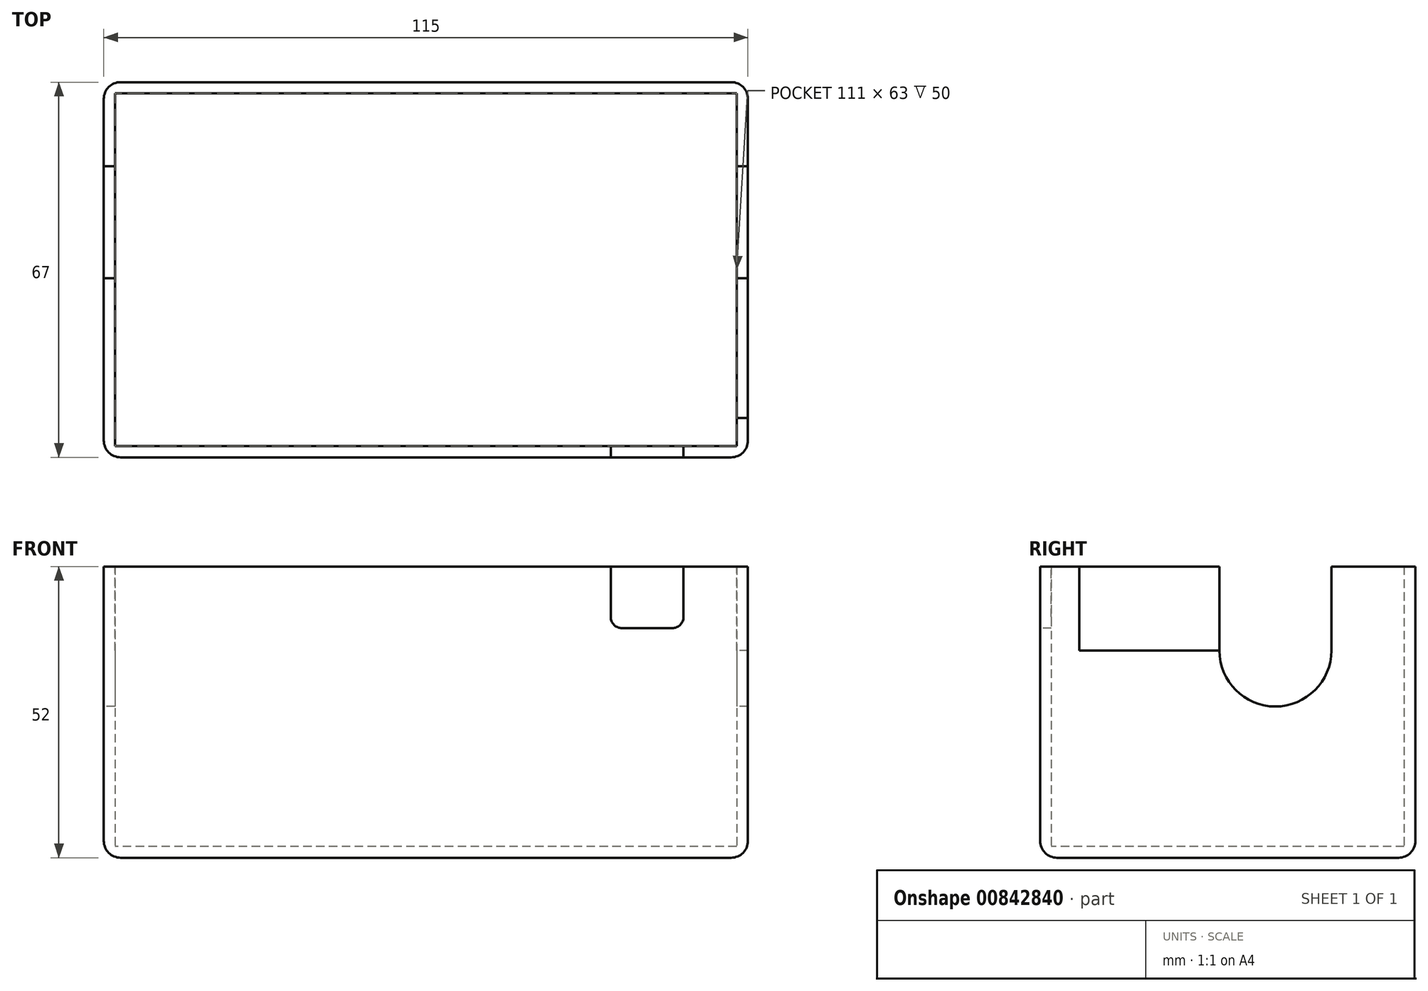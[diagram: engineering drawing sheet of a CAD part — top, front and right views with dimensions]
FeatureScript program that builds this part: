
annotation { "Feature Type Name" : "Feature", "Feature Type Description" : "" }
export const myFeature = defineFeature(function(context is Context, id is Id, definition is map)
    precondition{}
    {
        {
            var Q0;
            Q0=qCreatedBy(makeId("Top.planeOp"),FACE);
            var sketch = newSketch(context, id + "F0", { "sketchPlane" : qUnion([Q0])});
            skLineSegment(sketch, "E0.bottom", {"start": v(57.5, 33.5) * mm, "end": v(-57.5, 33.5) * mm});
            skLineSegment(sketch, "E0.top", {"start": v(57.5, -33.5) * mm, "end": v(-57.5, -33.5) * mm});
            skLineSegment(sketch, "E0.left", {"start": v(57.5, 33.5) * mm, "end": v(57.5, -33.5) * mm});
            skLineSegment(sketch, "E0.right", {"start": v(-57.5, 33.5) * mm, "end": v(-57.5, -33.5) * mm});
            skPoint(sketch, "E0.middle", {"position": v(0, 0) * mm});
            skSolve(sketch);
        }
        {
            var Q0;
            Q0=makeQuery(id+"F0.imprint","IMPRINT",FACE,{"disambiguationData":[TD([[makeQuery(id+"F0.imprint","IMPRINT",EDGE,{"derivedFrom":sQuery(id+"F0.wireOp",EDGE,"E0.bottom")}),1.0]])]});
            extrude(context, id + "F1", {"entities" : qUnion([Q0]), "depth" : 52 * mm, "offsetDistance" : 25 * mm});
        }
        {
            var Q0;
            Q0=makeQuery(id+"F1.opExtrude","CAP_FACE",FACE,{"disambiguationData":[OSD([sQuery(id+"F0.wireOp",EDGE,"E0.bottom"),sQuery(id+"F0.wireOp",EDGE,"E0.top"),sQuery(id+"F0.wireOp",EDGE,"E0.left"),sQuery(id+"F0.wireOp",EDGE,"E0.right")])],"isStart":false});
            shell(context, id + "F2", {"entities" : qUnion([Q0]), "thickness" : 2 * mm});
        }
        {
            var Q0;
            Q0=makeQuery(id+"F1.opExtrude","SWEPT_EDGE",EDGE,{"disambiguationData":[OSD([sQuery(id+"F0.wireOp",EDGE,"E0.bottom"),sQuery(id+"F0.wireOp",EDGE,"E0.left")])]});
            var Q1;
            Q1=makeQuery(id+"F1.opExtrude","SWEPT_EDGE",EDGE,{"disambiguationData":[OSD([sQuery(id+"F0.wireOp",EDGE,"E0.top"),sQuery(id+"F0.wireOp",EDGE,"E0.left")])]});
            var Q2;
            Q2=makeQuery(id+"F1.opExtrude","SWEPT_EDGE",EDGE,{"disambiguationData":[OSD([sQuery(id+"F0.wireOp",EDGE,"E0.top"),sQuery(id+"F0.wireOp",EDGE,"E0.right")])]});
            var Q3;
            Q3=makeQuery(id+"F1.opExtrude","SWEPT_EDGE",EDGE,{"disambiguationData":[OSD([sQuery(id+"F0.wireOp",EDGE,"E0.bottom"),sQuery(id+"F0.wireOp",EDGE,"E0.right")])]});
            var Q4;
            Q4=makeQuery(id+"F1.opExtrude","CAP_EDGE",EDGE,{"disambiguationData":[OSD([sQuery(id+"F0.wireOp",EDGE,"E0.right")])],"isStart":true});
            var Q5;
            Q5=makeQuery(id+"F1.opExtrude","CAP_EDGE",EDGE,{"disambiguationData":[OSD([sQuery(id+"F0.wireOp",EDGE,"E0.top")])],"isStart":true});
            var Q6;
            Q6=makeQuery(id+"F1.opExtrude","CAP_EDGE",EDGE,{"disambiguationData":[OSD([sQuery(id+"F0.wireOp",EDGE,"E0.bottom")])],"isStart":true});
            var Q7;
            Q7=makeQuery(id+"F1.opExtrude","CAP_EDGE",EDGE,{"disambiguationData":[OSD([sQuery(id+"F0.wireOp",EDGE,"E0.left")])],"isStart":true});
            fillet(context, id + "F3", {"entities" : qUnion([Q0, Q1, Q2, Q3, Q4, Q5, Q6, Q7]), "radius" : 3 * mm, "tangentPropagation" : true, "allowEdgeOverflow" : false});
        }
        {
            var Q0;
            Q0=makeQuery(id+"F1.opExtrude","SWEPT_FACE",FACE,{"disambiguationData":[OSD([sQuery(id+"F0.wireOp",EDGE,"E0.right")])]});
            var sketch = newSketch(context, id + "F4", { "sketchPlane" : qUnion([Q0])});
            skLineSegment(sketch, "E1", {"start": v(-33.5, 52) * mm, "end": v(-8.5, 52) * mm});
            skLineSegment(sketch, "E2", {"start": v(-8.5, 52) * mm, "end": v(-8.5, 37) * mm});
            skArc(sketch, "E3", {"start": v(-18.5, 37) * mm, "mid": v(-8.5, 27) * mm, "end": v(1.5, 37) * mm});
            skLineSegment(sketch, "E4", {"start": v(-18.5, 52) * mm, "end": v(-18.5, 37) * mm});
            skLineSegment(sketch, "E5", {"start": v(1.5, 52) * mm, "end": v(1.5, 37) * mm});
            skSolve(sketch);
        }
        {
            var Q0;
            Q0=makeQuery(id+"F4.imprint","IMPRINT",FACE,{"disambiguationData":[TD([[makeQuery(id+"F4.imprint","IMPRINT",EDGE,{"derivedFrom":sQuery(id+"F4.wireOp",EDGE,"E3")}),1.0]])]});
            var Q1;
            Q1=makeQuery(id+"F1.opExtrude","SWEPT_FACE",FACE,{"disambiguationData":[OSD([sQuery(id+"F0.wireOp",EDGE,"E0.left")])]});
            extrude(context, id + "F5", {"entities" : qUnion([Q0]), "operationType" : NewBodyOperationType.REMOVE, "endBound" : BoundingType.UP_TO_SURFACE, "oppositeDirection" : true, "depth" : 25 * mm, "endBoundEntityFace" : qUnion([Q1]), "offsetDistance" : 25 * mm});
        }
        {
            var Q0;
            Q0=makeQuery(id+"F1.opExtrude","SWEPT_FACE",FACE,{"disambiguationData":[OSD([sQuery(id+"F0.wireOp",EDGE,"E0.left")])]});
            var sketch = newSketch(context, id + "F6", { "sketchPlane" : qUnion([Q0])});
            skLineSegment(sketch, "E6", {"start": v(-1.5, 52) * mm, "end": v(-26.5, 52) * mm});
            skLineSegment(sketch, "E7", {"start": v(-26.5, 52) * mm, "end": v(-26.5, 37) * mm});
            skLineSegment(sketch, "E8", {"start": v(-26.5, 37) * mm, "end": v(-1.5, 37) * mm});
            skSolve(sketch);
        }
        {
            var Q0;
            Q0=makeQuery(id+"F6.imprint","IMPRINT",FACE,{"disambiguationData":[TD([[makeQuery(id+"F6.imprint","IMPRINT",EDGE,{"derivedFrom":sQuery(id+"F6.wireOp",EDGE,"E6")}),1.0]])]});
            var Q1;
            Q1=makeQuery(id+"F2.opShell","OFFSET_FACE",FACE,{"disambiguationData":[OSD([sQuery(id+"F0.wireOp",EDGE,"E0.left")])]});
            extrude(context, id + "F7", {"entities" : qUnion([Q0]), "operationType" : NewBodyOperationType.REMOVE, "endBound" : BoundingType.UP_TO_SURFACE, "oppositeDirection" : true, "depth" : 25 * mm, "endBoundEntityFace" : qUnion([Q1]), "offsetDistance" : 25 * mm});
        }
        {
            var Q0;
            Q0=makeQuery(id+"F1.opExtrude","SWEPT_FACE",FACE,{"disambiguationData":[OSD([sQuery(id+"F0.wireOp",EDGE,"E0.top")])]});
            var sketch = newSketch(context, id + "F8", { "sketchPlane" : qUnion([Q0])});
            skLineSegment(sketch, "E9.bottom", {"start": v(33, 52) * mm, "end": v(46, 52) * mm});
            skLineSegment(sketch, "E9.top", {"start": v(35, 41) * mm, "end": v(44, 41) * mm});
            skLineSegment(sketch, "E9.left", {"start": v(33, 52) * mm, "end": v(33, 43) * mm});
            skLineSegment(sketch, "E9.right", {"start": v(46, 52) * mm, "end": v(46, 43) * mm});
            skLineSegment(sketch, "E10", {"start": v(46, 52) * mm, "end": v(57.5, 52) * mm});
            skPoint(sketch, "E11.visualSharp", {"position": v(46, 41) * mm});
            skArc(sketch, "E11.filletArc", {"start": v(44, 41) * mm, "mid": v(45.41, 41.59) * mm, "end": v(46, 43) * mm});
            skPoint(sketch, "E12.visualSharp", {"position": v(33, 41) * mm});
            skArc(sketch, "E12.filletArc", {"start": v(33, 43) * mm, "mid": v(33.59, 41.59) * mm, "end": v(35, 41) * mm});
            skSolve(sketch);
        }
        {
            var Q0;
            Q0=makeQuery(id+"F8.imprint","IMPRINT",FACE,{"disambiguationData":[TD([[makeQuery(id+"F8.imprint","IMPRINT",EDGE,{"derivedFrom":sQuery(id+"F8.wireOp",EDGE,"E9.bottom")}),1.0]])]});
            var Q1;
            Q1=makeQuery(id+"F2.opShell","OFFSET_FACE",FACE,{"disambiguationData":[OSD([sQuery(id+"F0.wireOp",EDGE,"E0.top")])]});
            extrude(context, id + "F9", {"entities" : qUnion([Q0]), "operationType" : NewBodyOperationType.REMOVE, "endBound" : BoundingType.UP_TO_SURFACE, "oppositeDirection" : true, "depth" : 25 * mm, "endBoundEntityFace" : qUnion([Q1]), "offsetDistance" : 25 * mm});
        }
    });
